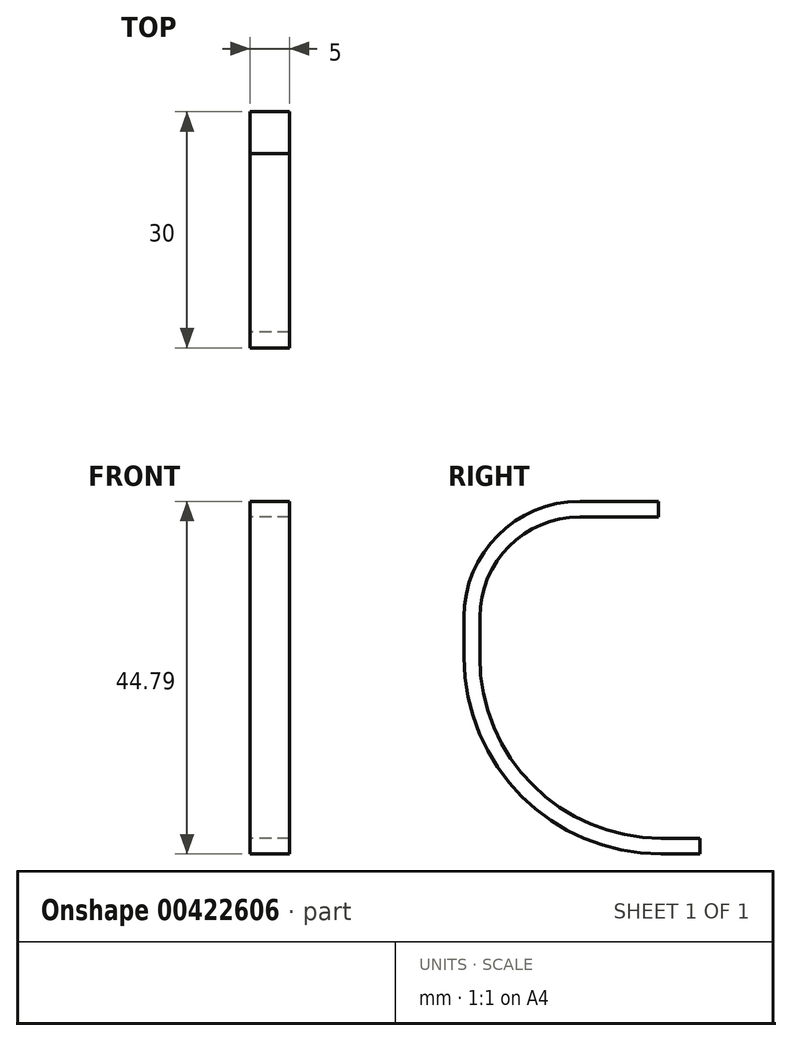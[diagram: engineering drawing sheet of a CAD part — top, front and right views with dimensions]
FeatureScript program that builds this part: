
annotation { "Feature Type Name" : "Feature", "Feature Type Description" : "" }
export const myFeature = defineFeature(function(context is Context, id is Id, definition is map)
    precondition{}
    {
        {
            var Q0;
            Q0=qCreatedBy(makeId("Right.planeOp"),FACE);
            var sketch = newSketch(context, id + "F0", { "sketchPlane" : qUnion([Q0])});
            skLineSegment(sketch, "E0", {"start": v(9.72, -0.2) * mm, "end": v(9.72, -5.3) * mm});
            skLineSegment(sketch, "E1", {"start": v(22.42, 12.5) * mm, "end": v(32.42, 12.5) * mm});
            skArc(sketch, "E2", {"start": v(22.42, 12.5) * mm, "mid": v(13.44, 8.78) * mm, "end": v(9.72, -0.2) * mm});
            skArc(sketch, "E3", {"start": v(9.72, -5.3) * mm, "mid": v(16.46, -21.56) * mm, "end": v(32.72, -28.3) * mm});
            skLineSegment(sketch, "E4.0", {"start": v(22.42, 14.5) * mm, "end": v(32.42, 14.5) * mm});
            skArc(sketch, "E4.1", {"start": v(22.42, 14.5) * mm, "mid": v(12.03, 10.2) * mm, "end": v(7.72, -0.2) * mm});
            skLineSegment(sketch, "E4.2", {"start": v(7.72, -0.2) * mm, "end": v(7.72, -5.3) * mm});
            skArc(sketch, "E4.3", {"start": v(7.72, -5.3) * mm, "mid": v(15.04, -22.97) * mm, "end": v(32.72, -30.3) * mm});
            skLineSegment(sketch, "E5", {"start": v(32.42, 14.5) * mm, "end": v(32.42, 12.5) * mm});
            skLineSegment(sketch, "E6", {"start": v(32.72, -28.3) * mm, "end": v(37.72, -28.3) * mm});
            skLineSegment(sketch, "E7", {"start": v(37.72, -28.3) * mm, "end": v(37.72, -30.3) * mm});
            skLineSegment(sketch, "E8", {"start": v(37.72, -30.3) * mm, "end": v(32.72, -30.3) * mm});
            skSolve(sketch);
        }
        {
            var Q0;
            Q0=makeQuery(id+"F0.imprint","IMPRINT",FACE,{"disambiguationData":[TD([[makeQuery(id+"F0.imprint","IMPRINT",EDGE,{"derivedFrom":sQuery(id+"F0.wireOp",EDGE,"E0")}),-1.0]])]});
            extrude(context, id + "F1", {"entities" : qUnion([Q0]), "depth" : 5 * mm});
        }
    });
